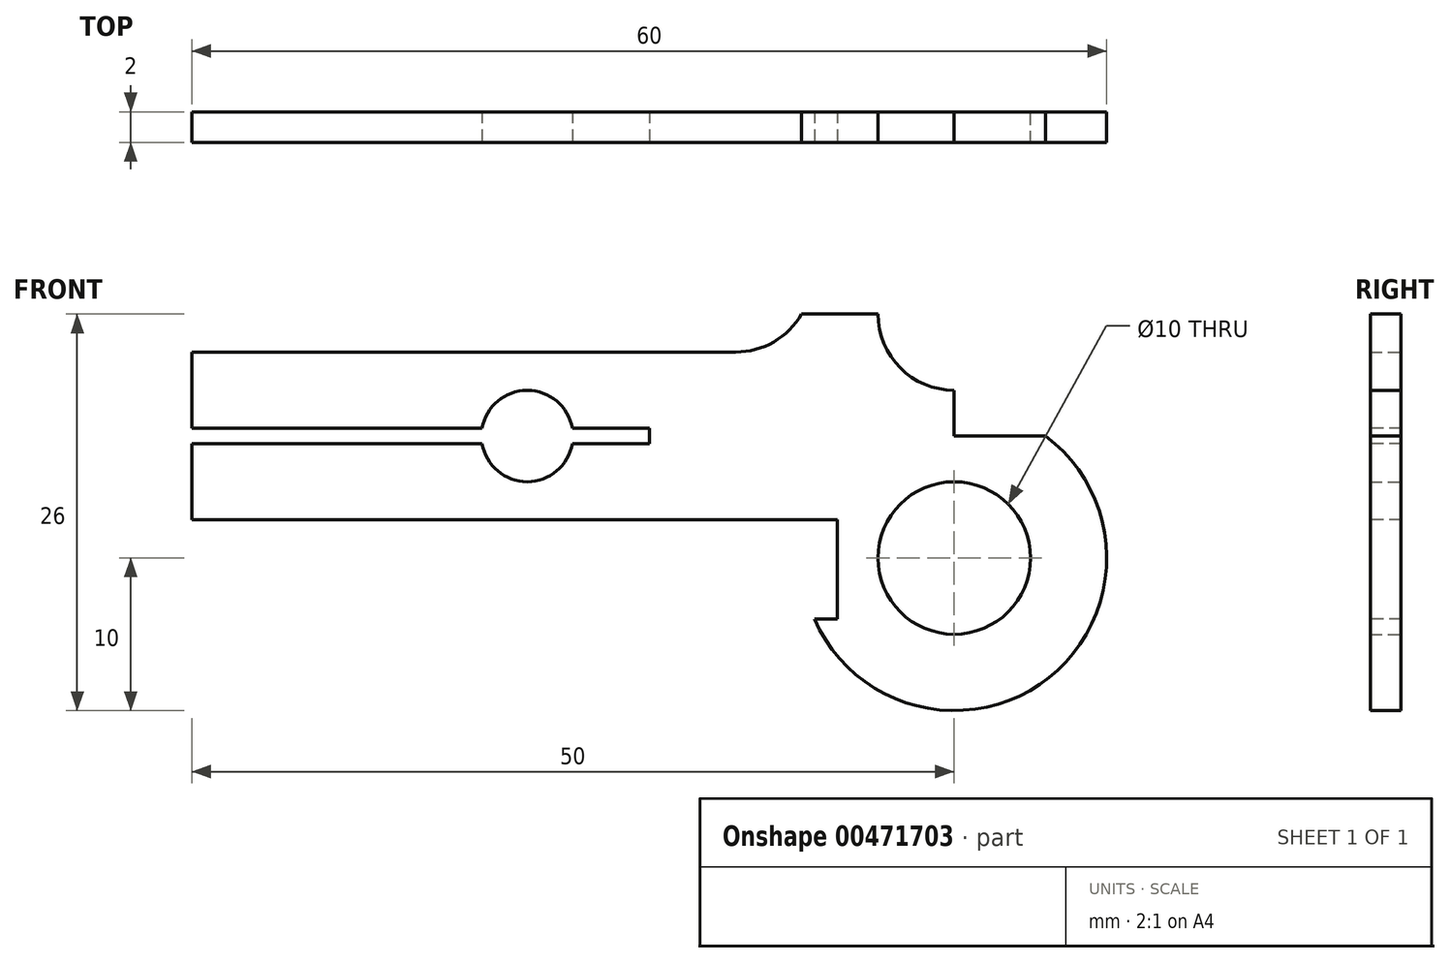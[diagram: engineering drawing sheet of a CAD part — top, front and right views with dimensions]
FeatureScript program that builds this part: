
annotation { "Feature Type Name" : "Feature", "Feature Type Description" : "" }
export const myFeature = defineFeature(function(context is Context, id is Id, definition is map)
    precondition{}
    {
        {
            var Q0;
            Q0=qCreatedBy(makeId("Front.planeOp"),FACE);
            var sketch = newSketch(context, id + "F0", { "sketchPlane" : qUnion([Q0])});
            skLineSegment(sketch, "E0.bottom", {"start": v(0, 0) * mm, "end": v(40, 0) * mm});
            skLineSegment(sketch, "E0.top", {"start": v(0, 11) * mm, "end": v(40, 11) * mm});
            skLineSegment(sketch, "E0.left", {"start": v(0, 0) * mm, "end": v(0, 11) * mm});
            skLineSegment(sketch, "E0.right", {"start": v(40, 0) * mm, "end": v(40, 11) * mm});
            skCircle(sketch, "E1", {"center": v(50, -2.5) * mm, "radius": 10 * mm});
            skCircle(sketch, "E2", {"center": v(50, 13.5) * mm, "radius": 10 * mm});
            skCircle(sketch, "E3", {"center": v(50, -2.5) * mm, "radius": 5 * mm});
            skCircle(sketch, "E4", {"center": v(50, 13.5) * mm, "radius": 5 * mm});
            skCircle(sketch, "E5", {"center": v(22, 5.5) * mm, "radius": 3 * mm});
            skPoint(sketch, "E5.centerSnap0", {"position": v(0, 5.5) * mm});
            skLineSegment(sketch, "E6", {"start": v(0, 5.5) * mm, "end": v(70.53, 5.5) * mm});
            skLineSegment(sketch, "E7.bottom", {"start": v(40, -2.5) * mm, "end": v(50, -2.5) * mm});
            skLineSegment(sketch, "E7.top", {"start": v(40, 13.5) * mm, "end": v(50, 13.5) * mm});
            skLineSegment(sketch, "E7.left", {"start": v(40, -2.5) * mm, "end": v(40, 13.5) * mm});
            skLineSegment(sketch, "E7.right", {"start": v(50, -2.5) * mm, "end": v(50, 13.5) * mm});
            skSolve(sketch);
        }
        {
            var Q0;
            Q0=makeQuery(id+"F0.imprint","IMPRINT",FACE,{"disambiguationData":[TD([[makeQuery(id+"F0.imprint","IMPRINT",EDGE,{"derivedFrom":sQuery(id+"F0.wireOp",EDGE,"E0.bottom")}),1.0]])]});
            var Q1;
            {var subQ0=sQuery(id+"F0.wireOp",EDGE,"E0.right");Q1=makeQuery(id+"F0.imprint","IMPRINT",FACE,{"disambiguationData":[TD([[makeQuery(id+"F0.imprint","IMPRINT",EDGE,{"derivedFrom":subQ0}),-1.0]])]});}
            var Q2;
            {var subQ0=sQuery(id+"F0.wireOp",EDGE,"E2");var subQ2=sQuery(id+"F0.wireOp",EDGE,"E1");var subQ3=makeQuery(id+"F0.imprint","INTERSECT",VERTEX,{"disambiguationData":[OD(0.0)],"derivedFrom":[subQ2,subQ0]});Q2=makeQuery(id+"F0.imprint","IMPRINT",FACE,{"disambiguationData":[TD([[makeQuery(id+"F0.imprint","IMPRINT",EDGE,{"disambiguationData":[TD([[subQ3,-1.0]])],"derivedFrom":subQ2}),-1.0]])]});}
            var Q3;
            {var subQ0=sQuery(id+"F0.wireOp",EDGE,"E2");var subQ1=sQuery(id+"F0.wireOp",EDGE,"E1");var subQ2=makeQuery(id+"F0.imprint","INTERSECT",VERTEX,{"disambiguationData":[OD(0.0)],"derivedFrom":[subQ1,subQ0]});Q3=makeQuery(id+"F0.imprint","IMPRINT",FACE,{"disambiguationData":[TD([[makeQuery(id+"F0.imprint","IMPRINT",EDGE,{"disambiguationData":[TD([[subQ2,-1.0]])],"derivedFrom":subQ1}),1.0]])]});}
            var Q4;
            {var subQ0=sQuery(id+"F0.wireOp",EDGE,"E2");var subQ1=sQuery(id+"F0.wireOp",EDGE,"E1");var subQ2=makeQuery(id+"F0.imprint","INTERSECT",VERTEX,{"disambiguationData":[OD(1.0)],"derivedFrom":[subQ1,subQ0]});Q4=makeQuery(id+"F0.imprint","IMPRINT",FACE,{"disambiguationData":[TD([[makeQuery(id+"F0.imprint","IMPRINT",EDGE,{"disambiguationData":[TD([[subQ2,-1.0]])],"derivedFrom":subQ0}),-1.0]])]});}
            var Q5;
            {var subQ5=sQuery(id+"F0.wireOp",EDGE,"E0.top");Q5=makeQuery(id+"F0.imprint","IMPRINT",FACE,{"disambiguationData":[TD([[makeQuery(id+"F0.imprint","IMPRINT",EDGE,{"derivedFrom":subQ5}),-1.0]])]});}
            var Q6;
            {var subQ0=sQuery(id+"F0.wireOp",EDGE,"E3");var subQ1=sQuery(id+"F0.wireOp",EDGE,"E2");var subQ2=makeQuery(id+"F0.imprint","INTERSECT",VERTEX,{"disambiguationData":[OD(0.0)],"derivedFrom":[subQ1,subQ0]});Q6=makeQuery(id+"F0.imprint","IMPRINT",FACE,{"disambiguationData":[TD([[makeQuery(id+"F0.imprint","IMPRINT",EDGE,{"disambiguationData":[TD([[subQ2,1.0]])],"derivedFrom":subQ0}),-1.0]])]});}
            var Q7;
            {var subQ0=sQuery(id+"F0.wireOp",EDGE,"E7.left");var subQ1=sQuery(id+"F0.wireOp",EDGE,"E7.top");var subQ2=makeQuery(id+"F0.imprint","INTERSECT",VERTEX,{"derivedFrom":[subQ1,subQ0]});Q7=makeQuery(id+"F0.imprint","IMPRINT",FACE,{"disambiguationData":[TD([[makeQuery(id+"F0.imprint","IMPRINT",EDGE,{"disambiguationData":[TD([[subQ2,-1.0]])],"derivedFrom":subQ1}),-1.0]])]});}
            var Q8;
            {var subQ0=sQuery(id+"F0.wireOp",EDGE,"E7.right");var subQ3=sQuery(id+"F0.wireOp",EDGE,"E6");var subQ5=makeQuery(id+"F0.imprint","INTERSECT",VERTEX,{"derivedFrom":[subQ3,subQ0]});Q8=makeQuery(id+"F0.imprint","IMPRINT",FACE,{"disambiguationData":[TD([[makeQuery(id+"F0.imprint","IMPRINT",EDGE,{"disambiguationData":[TD([[subQ5,1.0]])],"derivedFrom":subQ3}),1.0]])]});}
            var Q9;
            {var subQ0=sQuery(id+"F0.wireOp",EDGE,"E6");var subQ3=sQuery(id+"F0.wireOp",EDGE,"E7.right");var subQ5=makeQuery(id+"F0.imprint","INTERSECT",VERTEX,{"derivedFrom":[subQ0,subQ3]});Q9=makeQuery(id+"F0.imprint","IMPRINT",FACE,{"disambiguationData":[TD([[makeQuery(id+"F0.imprint","IMPRINT",EDGE,{"disambiguationData":[TD([[subQ5,1.0]])],"derivedFrom":subQ0}),-1.0]])]});}
            var Q10;
            {var subQ0=sQuery(id+"F0.wireOp",EDGE,"E7.left");var subQ1=sQuery(id+"F0.wireOp",EDGE,"E2");var subQ2=makeQuery(id+"F0.imprint","INTERSECT",VERTEX,{"derivedFrom":[subQ1,subQ0]});Q10=makeQuery(id+"F0.imprint","IMPRINT",FACE,{"disambiguationData":[TD([[makeQuery(id+"F0.imprint","IMPRINT",EDGE,{"disambiguationData":[TD([[subQ2,1.0]])],"derivedFrom":subQ0}),-1.0]])]});}
            var Q11;
            {var subQ1=sQuery(id+"F0.wireOp",EDGE,"E0.top");var subQ6=sQuery(id+"F0.wireOp",EDGE,"E0.left");var subQ11=makeQuery(id+"F0.imprint","INTERSECT",VERTEX,{"derivedFrom":[subQ1,subQ6]});Q11=makeQuery(id+"F0.imprint","IMPRINT",FACE,{"disambiguationData":[TD([[makeQuery(id+"F0.imprint","IMPRINT",EDGE,{"disambiguationData":[TD([[subQ11,-1.0]])],"derivedFrom":subQ1}),-1.0]])]});}
            var Q12;
            {var subQ5=sQuery(id+"F0.wireOp",EDGE,"E0.bottom");var subQ9=sQuery(id+"F0.wireOp",EDGE,"E0.left");var subQ10=makeQuery(id+"F0.imprint","INTERSECT",VERTEX,{"derivedFrom":[subQ5,subQ9]});Q12=makeQuery(id+"F0.imprint","IMPRINT",FACE,{"disambiguationData":[TD([[makeQuery(id+"F0.imprint","IMPRINT",EDGE,{"disambiguationData":[TD([[subQ10,-1.0]])],"derivedFrom":subQ5}),1.0]])]});}
            var Q13;
            {var subQ0=sQuery(id+"F0.wireOp",EDGE,"E6");var subQ3=sQuery(id+"F0.wireOp",EDGE,"E7.right");var subQ5=makeQuery(id+"F0.imprint","INTERSECT",VERTEX,{"derivedFrom":[subQ0,subQ3]});Q13=makeQuery(id+"F0.imprint","IMPRINT",FACE,{"disambiguationData":[TD([[makeQuery(id+"F0.imprint","IMPRINT",EDGE,{"disambiguationData":[TD([[subQ5,-1.0]])],"derivedFrom":subQ0}),-1.0]])]});}
            var Q14;
            {var subQ0=sQuery(id+"F0.wireOp",EDGE,"E7.left");var subQ1=sQuery(id+"F0.wireOp",EDGE,"E1");var subQ2=makeQuery(id+"F0.imprint","INTERSECT",VERTEX,{"derivedFrom":[subQ1,subQ0]});Q14=makeQuery(id+"F0.imprint","IMPRINT",FACE,{"disambiguationData":[TD([[makeQuery(id+"F0.imprint","IMPRINT",EDGE,{"disambiguationData":[TD([[subQ2,-1.0]])],"derivedFrom":subQ0}),-1.0]])]});}
            extrude(context, id + "F1", {"entities" : qUnion([Q0, Q1, Q2, Q3, Q4, Q5, Q6, Q7, Q8, Q9, Q10, Q11, Q12, Q13, Q14]), "depth" : 2 * mm, "offsetDistance" : 25 * mm});
        }
        {
            var Q0;
            Q0=makeQuery(id+"F1.opExtrude","SWEPT_EDGE",EDGE,{"disambiguationData":[OSD([sQuery(id+"F0.wireOp",EDGE,"E0.top"),sQuery(id+"F0.wireOp",EDGE,"E0.right"),sQuery(id+"F0.wireOp",EDGE,"E2")])]});
            var Q1;
            Q1=makeQuery(id+"F1.opExtrude","SWEPT_EDGE",EDGE,{"disambiguationData":[OSD([sQuery(id+"F0.wireOp",EDGE,"E0.bottom"),sQuery(id+"F0.wireOp",EDGE,"E0.right"),sQuery(id+"F0.wireOp",EDGE,"E1")])]});
            fillet(context, id + "F2", {"entities" : qUnion([Q0, Q1]), "radius" : 5 * mm, "tangentPropagation" : true, "allowEdgeOverflow" : false});
        }
        {
            var Q0;
            Q0=makeQuery(id+"F1.opExtrude","CAP_FACE",FACE,{"disambiguationData":[OSD([sQuery(id+"F0.wireOp",EDGE,"E0.bottom"),sQuery(id+"F0.wireOp",EDGE,"E0.top"),sQuery(id+"F0.wireOp",EDGE,"E0.left"),sQuery(id+"F0.wireOp",EDGE,"E1"),sQuery(id+"F0.wireOp",EDGE,"E2"),sQuery(id+"F0.wireOp",EDGE,"E3"),sQuery(id+"F0.wireOp",EDGE,"E4"),sQuery(id+"F0.wireOp",EDGE,"E5"),sQuery(id+"F0.wireOp",EDGE,"E7.left")])],"isStart":false});
            var sketch = newSketch(context, id + "F3", { "sketchPlane" : qUnion([Q0])});
            skLineSegment(sketch, "E8.bottom", {"start": v(0, 6) * mm, "end": v(30, 6) * mm});
            skLineSegment(sketch, "E9", {"start": v(0, 6) * mm, "end": v(0, 5) * mm});
            skLineSegment(sketch, "E10", {"start": v(0, 5) * mm, "end": v(30, 5) * mm});
            skLineSegment(sketch, "E11", {"start": v(30, 6) * mm, "end": v(30, 5) * mm});
            skSolve(sketch);
        }
        {
            var Q0;
            {var subQ0=sQuery(id+"F3.wireOp",EDGE,"E8.left");Q0=makeQuery(id+"F3.imprint","IMPRINT",FACE,{"disambiguationData":[TD([[makeQuery(id+"F3.imprint","IMPRINT",EDGE,{"derivedFrom":subQ0}),-1.0]])]});}
            var Q1;
            {var subQ0=sQuery(id+"F3.wireOp",EDGE,"E8.right");Q1=makeQuery(id+"F3.imprint","IMPRINT",FACE,{"disambiguationData":[TD([[makeQuery(id+"F3.imprint","IMPRINT",EDGE,{"derivedFrom":subQ0}),-1.0]])]});}
            var Q2;
            {var subQ0=sQuery(id+"F3.wireOp",EDGE,"E9");Q2=makeQuery(id+"F3.imprint","IMPRINT",FACE,{"disambiguationData":[TD([[makeQuery(id+"F3.imprint","IMPRINT",EDGE,{"derivedFrom":subQ0}),-1.0]])]});}
            var Q3;
            {var subQ0=sQuery(id+"F3.wireOp",EDGE,"E11");Q3=makeQuery(id+"F3.imprint","IMPRINT",FACE,{"disambiguationData":[TD([[makeQuery(id+"F3.imprint","IMPRINT",EDGE,{"derivedFrom":subQ0}),-1.0]])]});}
            extrude(context, id + "F4", {"entities" : qUnion([Q0, Q1, Q2, Q3]), "operationType" : NewBodyOperationType.REMOVE, "endBound" : BoundingType.UP_TO_NEXT, "oppositeDirection" : true, "depth" : 25 * mm});
        }
        {
            var Q0;
            Q0=makeQuery(id+"F1.opExtrude","CAP_FACE",FACE,{"disambiguationData":[OSD([sQuery(id+"F0.wireOp",EDGE,"E0.bottom"),sQuery(id+"F0.wireOp",EDGE,"E0.top"),sQuery(id+"F0.wireOp",EDGE,"E0.left"),sQuery(id+"F0.wireOp",EDGE,"E1"),sQuery(id+"F0.wireOp",EDGE,"E2"),sQuery(id+"F0.wireOp",EDGE,"E3"),sQuery(id+"F0.wireOp",EDGE,"E4"),sQuery(id+"F0.wireOp",EDGE,"E5"),sQuery(id+"F0.wireOp",EDGE,"E7.left")])],"isStart":false});
            var sketch = newSketch(context, id + "F5", { "sketchPlane" : qUnion([Q0])});
            skCircle(sketch, "E12", {"center": v(50, -2.5) * mm, "radius": 10 * mm});
            skLineSegment(sketch, "E13", {"start": v(35.2, 0) * mm, "end": v(42.33, 0) * mm});
            skLineSegment(sketch, "E14", {"start": v(35.2, 0) * mm, "end": v(40.83, -6.5) * mm});
            skLineSegment(sketch, "E15", {"start": v(40.83, -6.5) * mm, "end": v(42.33, -6.5) * mm});
            skLineSegment(sketch, "E16", {"start": v(42.33, 0) * mm, "end": v(42.33, -6.5) * mm});
            skSolve(sketch);
        }
        {
            var Q0;
            {var subQ6=sQuery(id+"F5.wireOp",EDGE,"mGd6iFxk-vmMK-pAj5-A2W1-8Xiw3Hgm5lPV");Q0=makeQuery(id+"F5.imprint","IMPRINT",FACE,{"disambiguationData":[TD([[makeQuery(id+"F5.imprint","IMPRINT",EDGE,{"derivedFrom":subQ6}),-1.0]])]});}
            var Q1;
            {var subQ1=sQuery(id+"F0.wireOp",EDGE,"E7.left");var subQ2=sQuery(id+"F0.wireOp",EDGE,"E0.bottom");var subQ3=makeQuery(id+"F2.opFillet","BLEND_EDGE",EDGE,{"blendedFrom":[makeQuery(id+"F1.opExtrude","SWEPT_EDGE",EDGE,{"disambiguationData":[OSD([subQ2,subQ1])]}),makeQuery(id+"F1.opExtrude","CAP_FACE",FACE,{"disambiguationData":[OSD([subQ2,sQuery(id+"F0.wireOp",EDGE,"E0.top"),sQuery(id+"F0.wireOp",EDGE,"E0.left"),sQuery(id+"F0.wireOp",EDGE,"E1"),sQuery(id+"F0.wireOp",EDGE,"E2"),sQuery(id+"F0.wireOp",EDGE,"E3"),sQuery(id+"F0.wireOp",EDGE,"E4"),sQuery(id+"F0.wireOp",EDGE,"E5"),subQ1])],"isStart":false})],"blendedInto":[makeQuery(id+"F1.opExtrude","CAP_FACE",FACE,{"disambiguationData":[OSD([subQ2,sQuery(id+"F0.wireOp",EDGE,"E0.top"),sQuery(id+"F0.wireOp",EDGE,"E0.left"),sQuery(id+"F0.wireOp",EDGE,"E1"),sQuery(id+"F0.wireOp",EDGE,"E2"),sQuery(id+"F0.wireOp",EDGE,"E3"),sQuery(id+"F0.wireOp",EDGE,"E4"),sQuery(id+"F0.wireOp",EDGE,"E5"),subQ1])],"isStart":false})]});Q1=makeQuery(id+"F5.imprint","IMPRINT",FACE,{"disambiguationData":[TD([[makeQuery(id+"F5.imprint","IMPRINT",EDGE,{"derivedFrom":subQ3}),1.0]])]});}
            var Q2;
            {var subQ4=sQuery(id+"F5.wireOp",EDGE,"E15");Q2=makeQuery(id+"F5.imprint","IMPRINT",FACE,{"disambiguationData":[TD([[makeQuery(id+"F5.imprint","IMPRINT",EDGE,{"derivedFrom":subQ4}),1.0]])]});}
            extrude(context, id + "F6", {"entities" : qUnion([Q0, Q1, Q2]), "operationType" : NewBodyOperationType.REMOVE, "oppositeDirection" : true, "depth" : 25 * mm, "offsetDistance" : 25 * mm});
        }
    });
